# Revit family: Vitra-Elite-IlluminatedMirrorCabinet-56779+56780+56781+56782+56783+56784+56785+56786+56787+56788+58170+58225
name_source: partatom
category: Furniture Systems
revit_build: Autodesk Revit 2017 (Build: 20160225_1515(x64)
units: mm (PartAtom-declared; Revit-internal decimal feet)

## family parameters
Cut with Voids When Loaded = No
Host = Face
OmniClass Number = 23.40.00.00
OmniClass Title = Equipment and Furnishings
Part Type = Normal
Room Calculation Point = No
Round Connector Dimension = Use Diameter
Shared = Yes

## types (1)
- MirrorCabinet(Illuminated)-Vitra-EliteSeries_56779
    Article No. (default) = 56779
    BIMobject category = Storage
    Construction Type = Wall Mounted
    Default Elevation = 1255 mm  [stored 4.11745 ft]
    Depth(mm) = 150 mm
    Description = Elite Illuminated Mirror Cabinet
    Design country = Turkey
    Height(mm) = 700 mm  [stored 2.29659 ft]
    IFC Classification = Furnishing Element
    Lighting Type = Sandblasted Led Lighting
    Manufacturer = Vitra
    Manufacturer name = Vitra
    Masterformat 2014 Code = 41 53 13
    Masterformat 2014 Description = Storage Cabinets
    Model = 56779
    NBS Referans Code = 35-75-08
    NBS Referans Description = Bathroom Cabinets
    Nominal height = 0.000
    Nominal width = 0.000
    OmniClass Code = 23-25 53 11 13 11
    OmniClass Description = Medicine Cabinets
    Primary Material = Vitra-Mirror
    Product SKU = 56779
    Product certification = https://vitraglobal.com
    Product data url = https://www.vitra.com.tr
    Product family = Elite
    Product group = Bathroom Furniture
    Secondary Material = Vitra-Altın Kiraz
    Technical description = https://www.vitra.com.tr
    Thrid Material = Vitra-Light
    UNSPSC Code = 30161801
    UNSPSC Description = Bathroom cabinets
    URL = https://vitraglobal.com
    Uniclass 1.4 Code = L72141
    Uniclass 1.4 Description = Cabinets
    Uniclass 2.0 Code = PR-35-75-08
    Uniclass 2.0 Description = Bathroom Cabinets
    Uniclass 2015 Code = Pr_40_30_78_03
    Uniclass 2015 Name = Bathroom cabinets
    Uniformat II Code = E20
    Uniformat II Description = Furnishings
    Voltage = 220V
    Warranty Period (Year) = 2
    Weight Net (kg) = 36
    Width(mm) = 1000 mm  [stored 3.28084 ft]
    Youtube = https://www.youtube.com

note: [stored X ft] marks values corroborated as IEEE doubles in the binary element streams (Revit-internal decimal feet)

## geometry (parser evidence)
native form markers: Sweep x2
no freeform markers — native parametric forms only
